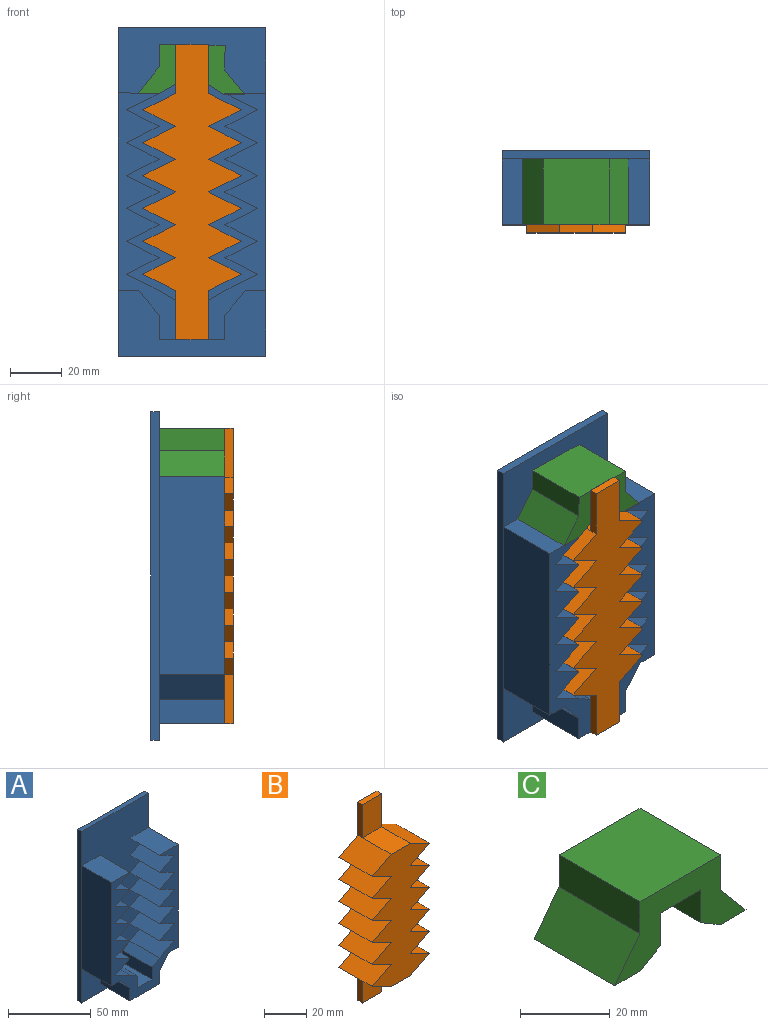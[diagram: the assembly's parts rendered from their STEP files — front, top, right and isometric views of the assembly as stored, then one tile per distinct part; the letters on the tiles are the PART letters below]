
ASSEMBLY  parts=3 mates=2
PART A: 48 faces, bbox 57.2x28.6x127 mm
  f0: plane 25.4x7.94mm, normal (0,0,-1), area 201.6mm2, adj f16,f17,f31,f37,f44
  f1: plane 25.4x15.88mm, normal (0.01,0,1), area 403.3mm2, adj f2,f15,f16,f37
  f2: plane 76.43x25.4mm, normal (-1,0,0), area 1941.3mm2, adj f1,f3,f16,f37
  f3: plane 25.4x7.94mm, normal (0,0,-1), area 201.6mm2, adj f2,f16,f37,f40
  f4: plane 25.4x12.7mm, normal (0.45,0,0.89), area 360.7mm2, adj f5,f16,f37,f39
  f5: plane 25.4x12.7mm, normal (0.45,0,-0.89), area 360.7mm2, adj f4,f6,f16,f37
  f6: plane 25.4x12.7mm, normal (0.45,0,0.89), area 360.7mm2, adj f5,f7,f16,f37
  f7: plane 25.4x12.7mm, normal (0.45,0,-0.89), area 360.7mm2, adj f6,f8,f16,f37
  f8: plane 25.4x12.7mm, normal (0.45,0,0.89), area 360.7mm2, adj f7,f9,f16,f37
  f9: plane 25.4x12.7mm, normal (0.45,0,-0.89), area 360.7mm2, adj f8,f10,f16,f37
  f10: plane 25.4x12.7mm, normal (0.45,0,0.89), area 360.7mm2, adj f9,f11,f16,f37
  f11: plane 25.4x12.7mm, normal (0.45,0,-0.89), area 360.7mm2, adj f10,f12,f16,f37
  f12: plane 25.4x12.7mm, normal (0.45,0,0.89), area 360.7mm2, adj f11,f13,f16,f37
  f13: plane 25.4x12.7mm, normal (0.45,0,-0.89), area 360.7mm2, adj f12,f14,f16,f37
  f14: plane 25.4x12.7mm, normal (0.45,0,0.89), area 360.7mm2, adj f13,f15,f16,f37
  f15: plane 25.4x12.7mm, normal (0.45,0,-0.89), area 360.7mm2, adj f1,f14,f16,f37
  f16: plane 95.48x57.15mm, normal (0,-1,0), area 1827.9mm2, adj f0,f1,f2,f3,f4,f5,f6,f7
  f17: plane 76.25x25.4mm, normal (1,0,0), area 1936.9mm2, adj f0,f16,f18,f31
  f18: plane 25.4x15.88mm, normal (0,0,1), area 403.2mm2, adj f16,f17,f19,f31,f37
  f19: plane 25.4x12.7mm, normal (-0.45,0,-0.89), area 360.7mm2, adj f16,f18,f20,f37
  f20: plane 25.4x12.7mm, normal (-0.45,0,0.89), area 360.7mm2, adj f16,f19,f21,f37
  f21: plane 25.4x12.7mm, normal (-0.45,0,-0.89), area 360.7mm2, adj f16,f20,f22,f37
  f22: plane 25.4x12.7mm, normal (-0.45,0,0.89), area 360.7mm2, adj f16,f21,f23,f37
  f23: plane 25.4x12.7mm, normal (-0.45,0,-0.89), area 360.7mm2, adj f16,f22,f24,f37
  f24: plane 25.4x12.7mm, normal (-0.45,0,0.89), area 360.7mm2, adj f16,f23,f25,f37
  f25: plane 25.4x12.7mm, normal (-0.45,0,-0.89), area 360.7mm2, adj f16,f24,f26,f37
  f26: plane 25.4x12.7mm, normal (-0.45,0,0.89), area 360.7mm2, adj f16,f25,f27,f37
  f27: plane 25.4x12.7mm, normal (-0.45,0,-0.89), area 360.7mm2, adj f16,f26,f28,f37
  f28: plane 25.4x12.7mm, normal (-0.45,0,0.89), area 360.7mm2, adj f16,f27,f29,f37
  f29: plane 25.4x12.7mm, normal (-0.45,0,-0.89), area 360.7mm2, adj f16,f28,f30,f37
  f30: plane 25.4x12.7mm, normal (-0.45,0,0.89), area 360.7mm2, adj f16,f29,f37,f45
  f31: plane 76.25x0.03mm, normal (0,1,0), area 2mm2, adj f0,f17,f18,f34
  f32: plane 127x3.18mm, normal (-1,0,0), area 403.2mm2, adj f33,f35,f36,f37
  f33: plane 57.15x3.18mm, normal (0,0,-1), area 181.5mm2, adj f32,f34,f36,f37
  f34: plane 127x3.18mm, normal (1,0,0), area 403.2mm2, adj f31,f33,f35,f36,f37
  f35: plane 57.15x3.18mm, normal (0,0,1), area 181.5mm2, adj f32,f34,f36,f37
  f36: plane 127x57.15mm, normal (0,1,0), area 7258mm2, adj f32,f33,f34,f35
  f37: plane 127x57.15mm, normal (0,-1,0), area 5432.2mm2, adj f0,f1,f2,f3,f4,f5,f6,f7
  f38: plane 25.4x8.89mm, normal (1,0,0), area 225.8mm2, adj f16,f37,f39,f47
  f39: plane 25.4x6.35mm, normal (0.51,0,0.86), area 188.1mm2, adj f4,f16,f37,f38
  f40: plane 25.4x9.53mm, normal (-0.77,0,-0.64), area 314.9mm2, adj f3,f16,f37,f41
  f41: plane 25.4x9.53mm, normal (-1,0,0), area 241.9mm2, adj f16,f37,f40,f42
  f42: plane 25.4x25.4mm, normal (0,0,-1), area 645.2mm2, adj f16,f37,f41,f43
  f43: plane 25.4x9.53mm, normal (1,0,0), area 241.9mm2, adj f16,f37,f42,f44
  f44: plane 25.4x9.53mm, normal (0.77,0,-0.64), area 314.9mm2, adj f0,f16,f37,f43
  f45: plane 25.4x6.35mm, normal (-0.51,0,0.86), area 188.1mm2, adj f16,f30,f37,f46
  f46: plane 25.4x8.89mm, normal (-1,0,0), area 225.8mm2, adj f16,f37,f45,f47
  f47: plane 25.4x12.7mm, normal (0,0,1), area 322.6mm2, adj f16,f37,f38,f46
PART B: 36 faces, bbox 38.1x22.2x114.3 mm
  f0: plane 22.23x12.7mm, normal (0.45,0,0.89), area 315.6mm2, adj f1,f25,f26,f27
  f1: plane 22.23x12.7mm, normal (0.45,0,-0.89), area 315.6mm2, adj f0,f2,f26,f27
  f2: plane 22.23x12.7mm, normal (0.45,0,0.89), area 315.6mm2, adj f1,f3,f26,f27
  f3: plane 22.23x12.7mm, normal (0.45,0,-0.89), area 315.6mm2, adj f2,f4,f26,f27
  f4: plane 22.23x12.7mm, normal (0.45,0,0.89), area 315.6mm2, adj f3,f5,f26,f27,f33
  f5: plane 19.05x12.7mm, normal (0,0,1), area 241.9mm2, adj f4,f6,f26,f35
  f6: plane 22.23x12.7mm, normal (-0.45,0,0.89), area 315.6mm2, adj f5,f7,f26,f27,f32
  f7: plane 22.23x12.7mm, normal (-0.45,0,-0.89), area 315.6mm2, adj f6,f8,f26,f27
  f8: plane 22.23x12.7mm, normal (-0.45,0,0.89), area 315.6mm2, adj f7,f9,f26,f27
  f9: plane 22.23x12.7mm, normal (-0.45,0,-0.89), area 315.6mm2, adj f8,f10,f26,f27
  f10: plane 22.23x12.7mm, normal (-0.45,0,0.89), area 315.6mm2, adj f9,f11,f26,f27
  f11: plane 22.23x12.7mm, normal (-0.45,0,-0.89), area 315.6mm2, adj f10,f12,f26,f27
  f12: plane 22.23x12.7mm, normal (-0.45,0,0.89), area 315.6mm2, adj f11,f13,f26,f27
  f13: plane 22.23x12.7mm, normal (-0.45,0,-0.89), area 315.6mm2, adj f12,f14,f26,f27
  f14: plane 22.23x12.7mm, normal (-0.45,0,0.89), area 315.6mm2, adj f13,f15,f26,f27
  f15: plane 22.23x12.7mm, normal (-0.45,0,-0.89), area 315.6mm2, adj f14,f16,f26,f27
  f16: plane 22.23x12.7mm, normal (-0.45,0,0.89), area 315.6mm2, adj f15,f17,f26,f27
  f17: plane 22.23x12.7mm, normal (-0.45,0,-0.89), area 315.6mm2, adj f16,f18,f26,f27,f31
  f18: plane 19.05x12.7mm, normal (0,0,-1), area 241.9mm2, adj f17,f19,f26,f30
  f19: plane 22.23x12.7mm, normal (0.45,0,-0.89), area 315.6mm2, adj f18,f20,f26,f27,f29
  f20: plane 22.23x12.7mm, normal (0.45,0,0.89), area 315.6mm2, adj f19,f21,f26,f27
  f21: plane 22.23x12.7mm, normal (0.45,0,-0.89), area 315.6mm2, adj f20,f22,f26,f27
  f22: plane 22.23x12.7mm, normal (0.45,0,0.89), area 315.6mm2, adj f21,f23,f26,f27
  f23: plane 22.23x12.7mm, normal (0.45,0,-0.89), area 315.6mm2, adj f22,f24,f26,f27
  f24: plane 22.23x12.7mm, normal (0.45,0,0.89), area 315.6mm2, adj f23,f25,f26,f27
  f25: plane 22.23x12.7mm, normal (0.45,0,-0.89), area 315.6mm2, adj f0,f24,f26,f27
  f26: plane 76.2x38.1mm, normal (0,-1,0), area 1935.5mm2, adj f0,f1,f2,f3,f4,f5,f6,f7
  f27: plane 114.3x38.1mm, normal (0,1,0), area 2419.3mm2, adj f0,f1,f2,f3,f4,f6,f7,f8
  f28: plane 12.7x3.18mm, normal (0,0,-1), area 40.3mm2, adj f27,f29,f30,f31
  f29: plane 19.05x3.18mm, normal (1,0,0), area 60.5mm2, adj f19,f27,f28,f30
  f30: plane 19.05x12.7mm, normal (0,-1,0), area 241.9mm2, adj f18,f28,f29,f31
  f31: plane 19.05x3.18mm, normal (-1,0,0), area 60.5mm2, adj f17,f27,f28,f30
  f32: plane 19.05x3.18mm, normal (-1,0,0), area 60.5mm2, adj f6,f27,f34,f35
  f33: plane 19.05x3.18mm, normal (1,0,0), area 60.5mm2, adj f4,f27,f34,f35
  f34: plane 12.7x3.18mm, normal (0,0,1), area 40.3mm2, adj f27,f32,f33,f35
  f35: plane 19.05x12.7mm, normal (0,-1,0), area 241.9mm2, adj f5,f32,f33,f34
PART C: 14 faces, bbox 41.3x25.4x18.9 mm
  f0: plane 25.4x6.16mm, normal (-0.51,0,-0.86), area 182.4mm2, adj f1,f11,f12,f13
  f1: plane 25.4x8.13mm, normal (0,0,-1), area 206.5mm2, adj f0,f2,f12,f13
  f2: plane 25.4x9.41mm, normal (0.76,0,0.64), area 312.7mm2, adj f1,f3,f12,f13
  f3: plane 25.4x9.53mm, normal (1,0,0), area 241.9mm2, adj f2,f4,f12,f13
  f4: plane 25.4x25.4mm, normal (0,0,1), area 645.2mm2, adj f3,f5,f12,f13
  f5: plane 25.4x8.71mm, normal (-1,0,0), area 221.2mm2, adj f4,f6,f12,f13
  f6: plane 25.4x10.23mm, normal (-0.79,0,0.61), area 328.8mm2, adj f5,f7,f12,f13
  f7: plane 25.4x8.13mm, normal (0,0,-1), area 206.5mm2, adj f6,f8,f12,f13
  f8: plane 25.4x6.16mm, normal (0.51,0,-0.86), area 182.4mm2, adj f7,f9,f12,f13
  f9: plane 25.4x8.89mm, normal (1,0,0), area 225.8mm2, adj f8,f10,f12,f13
  f10: plane 25.4x12.7mm, normal (0,0,-1), area 322.6mm2, adj f9,f11,f12,f13
  f11: plane 25.4x8.89mm, normal (-1,0,0), area 225.8mm2, adj f0,f10,f12,f13
  f12: plane 41.28x18.93mm, normal (0,-1,0), area 376.3mm2, adj f0,f1,f2,f3,f4,f5,f6,f7
  f13: plane 41.28x18.93mm, normal (0,1,0), area 376.3mm2, adj f0,f1,f2,f3,f4,f5,f6,f7
PLACE A t=(0,0,6.35)mm
PLACE B rot(axis=(1,0,0),180deg) t=(0,-28.57,82.55)mm
PLACE C rot(axis=(0,1,0),0.8deg) t=(-1.3,0,6.15)mm
MATE fastened A.f16 <-> B.f30  axis (0,-1,0) through (6.35,-25.4,101.6)mm
MATE fastened C.f7 <-> A.f1  axis (-0.01,0,-1) through (-6.35,-25.4,82.55)mm
